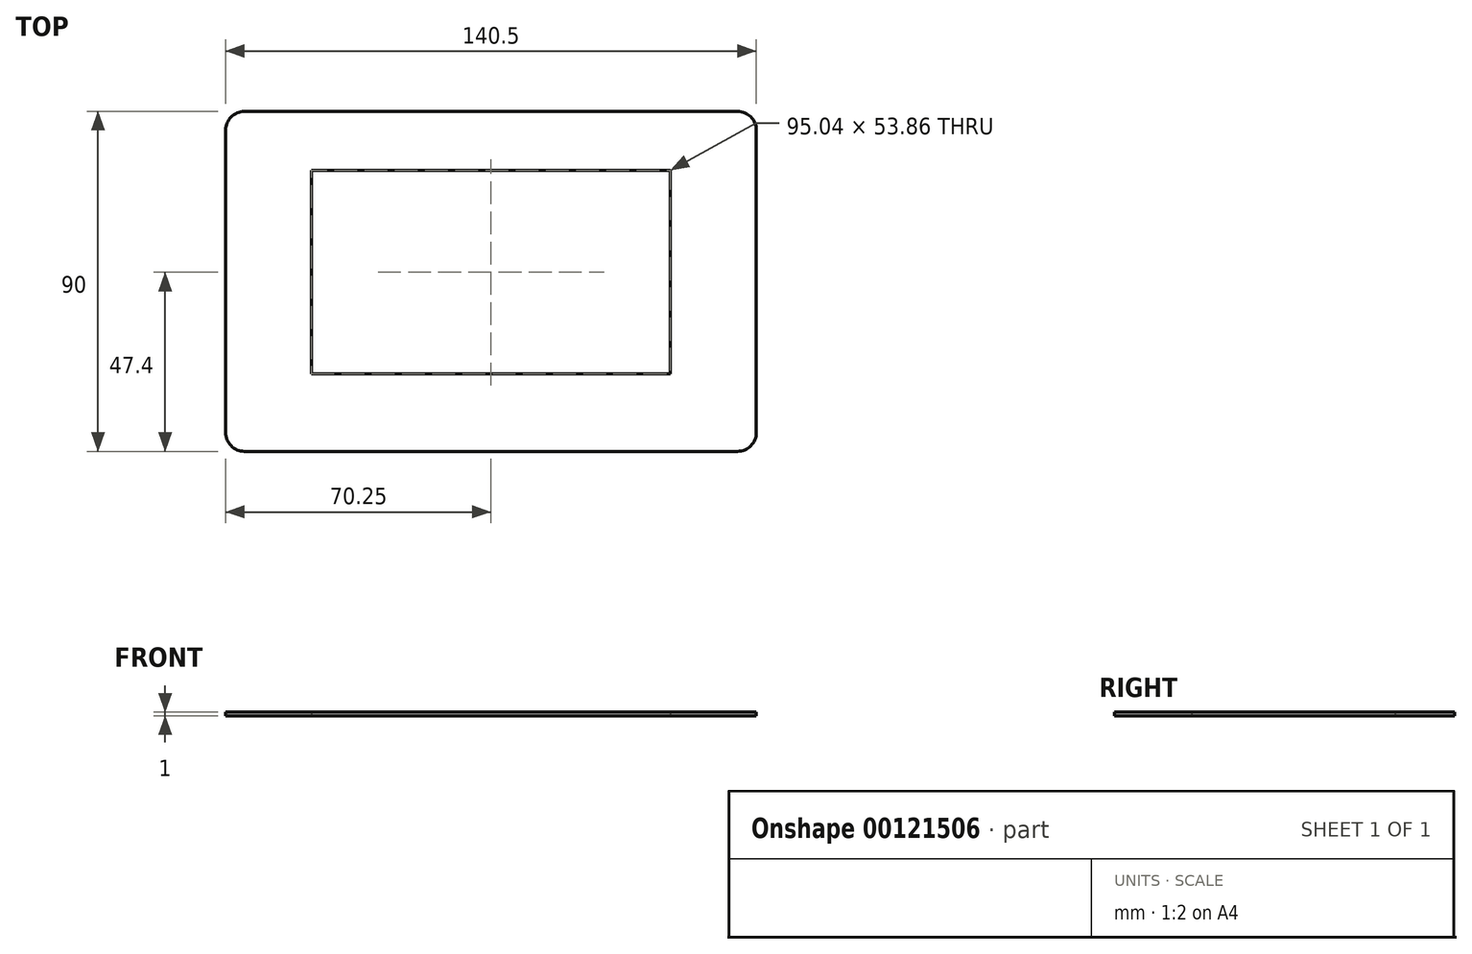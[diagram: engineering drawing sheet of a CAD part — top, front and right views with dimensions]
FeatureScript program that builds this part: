
annotation { "Feature Type Name" : "Feature", "Feature Type Description" : "" }
export const myFeature = defineFeature(function(context is Context, id is Id, definition is map)
    precondition{}
    {
        {
            var Q0;
            Q0=qCreatedBy(makeId("Top.planeOp"),FACE);
            var sketch = newSketch(context, id + "F0", { "sketchPlane" : qUnion([Q0])});
            skLineSegment(sketch, "E0.bottom", {"start": v(-60.25, 34.65) * mm, "end": v(60.25, 34.65) * mm});
            skLineSegment(sketch, "E0.top", {"start": v(-60.25, -34.65) * mm, "end": v(60.25, -34.65) * mm});
            skLineSegment(sketch, "E0.left", {"start": v(-60.25, 34.65) * mm, "end": v(-60.25, -34.65) * mm});
            skLineSegment(sketch, "E0.right", {"start": v(60.25, 34.65) * mm, "end": v(60.25, -34.65) * mm});
            skPoint(sketch, "E0.middle", {"position": v(0, 0) * mm});
            skLineSegment(sketch, "E1.bottom", {"start": v(-47.52, 29.33) * mm, "end": v(47.52, 29.33) * mm});
            skLineSegment(sketch, "E1.top", {"start": v(-47.52, -24.53) * mm, "end": v(47.52, -24.53) * mm});
            skLineSegment(sketch, "E1.left", {"start": v(-47.52, 29.33) * mm, "end": v(-47.52, -24.53) * mm});
            skLineSegment(sketch, "E1.right", {"start": v(47.52, 29.33) * mm, "end": v(47.52, -24.53) * mm});
            skLineSegment(sketch, "E2.bottom", {"start": v(-70.25, 45) * mm, "end": v(70.25, 45) * mm});
            skLineSegment(sketch, "E2.top", {"start": v(-70.25, -45) * mm, "end": v(70.25, -45) * mm});
            skLineSegment(sketch, "E2.left", {"start": v(-70.25, 45) * mm, "end": v(-70.25, -45) * mm});
            skLineSegment(sketch, "E2.right", {"start": v(70.25, 45) * mm, "end": v(70.25, -45) * mm});
            skSolve(sketch);
        }
        {
            var Q0;
            Q0=makeQuery(id+"F0.imprint","IMPRINT",FACE,{"disambiguationData":[TD([[makeQuery(id+"F0.imprint","IMPRINT",EDGE,{"derivedFrom":sQuery(id+"F0.wireOp",EDGE,"E0.bottom")}),1.0]])]});
            var Q1;
            Q1=makeQuery(id+"F0.imprint","IMPRINT",FACE,{"disambiguationData":[TD([[makeQuery(id+"F0.imprint","IMPRINT",EDGE,{"derivedFrom":sQuery(id+"F0.wireOp",EDGE,"E0.bottom")}),-1.0]])]});
            extrude(context, id + "F1", {"entities" : qUnion([Q0, Q1]), "depth" : 1 * mm});
        }
        {
            var Q0;
            Q0=makeQuery(id+"F1.opExtrude","SWEPT_EDGE",EDGE,{"disambiguationData":[OSD([sQuery(id+"F0.wireOp",EDGE,"E2.bottom"),sQuery(id+"F0.wireOp",EDGE,"E2.left")])]});
            var Q1;
            Q1=makeQuery(id+"F1.opExtrude","SWEPT_EDGE",EDGE,{"disambiguationData":[OSD([sQuery(id+"F0.wireOp",EDGE,"E2.top"),sQuery(id+"F0.wireOp",EDGE,"E2.left")])]});
            var Q2;
            Q2=makeQuery(id+"F1.opExtrude","SWEPT_EDGE",EDGE,{"disambiguationData":[OSD([sQuery(id+"F0.wireOp",EDGE,"E2.top"),sQuery(id+"F0.wireOp",EDGE,"E2.right")])]});
            var Q3;
            Q3=makeQuery(id+"F1.opExtrude","SWEPT_EDGE",EDGE,{"disambiguationData":[OSD([sQuery(id+"F0.wireOp",EDGE,"E2.bottom"),sQuery(id+"F0.wireOp",EDGE,"E2.right")])]});
            fillet(context, id + "F2", {"entities" : qUnion([Q0, Q1, Q2, Q3]), "radius" : 5 * mm, "tangentPropagation" : true, "allowEdgeOverflow" : false});
        }
    });
